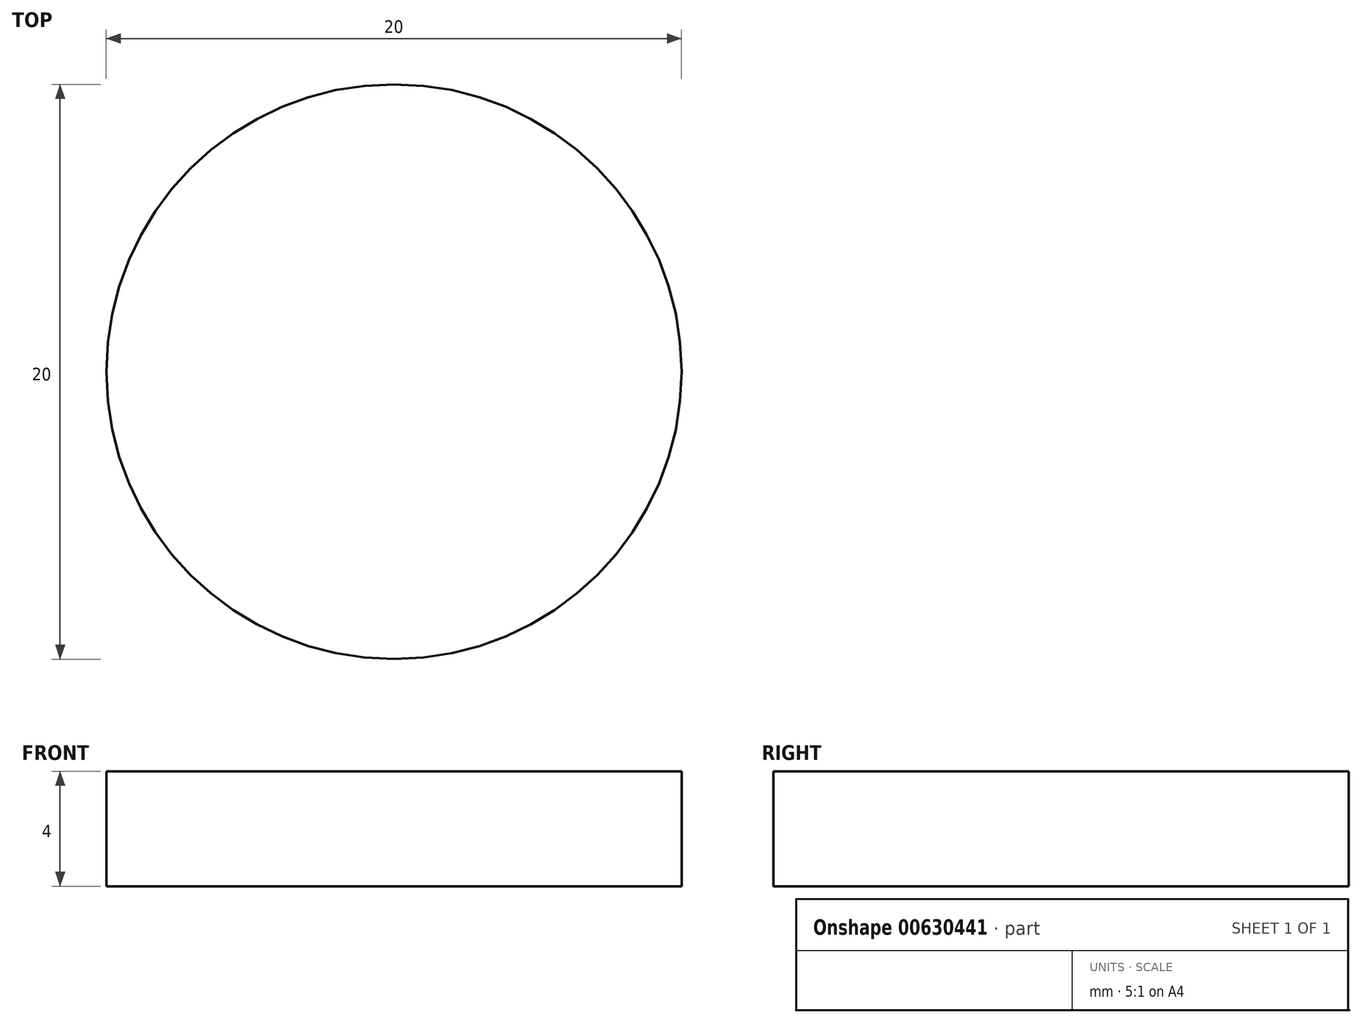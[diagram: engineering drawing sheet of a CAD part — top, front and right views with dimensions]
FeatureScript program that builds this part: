
annotation { "Feature Type Name" : "Feature", "Feature Type Description" : "" }
export const myFeature = defineFeature(function(context is Context, id is Id, definition is map)
    precondition{}
    {
        {
            var Q0;
            Q0=qCreatedBy(makeId("Top.planeOp"),FACE);
            var sketch = newSketch(context, id + "F0", { "sketchPlane" : qUnion([Q0])});
            skCircle(sketch, "E0", {"center": v(9.41, 17.38) * mm, "radius": 10 * mm});
            skSolve(sketch);
        }
        {
            var Q0;
            Q0=makeQuery(id+"F0.imprint","IMPRINT",FACE,{"disambiguationData":[TD([[makeQuery(id+"F0.imprint","IMPRINT",EDGE,{"derivedFrom":sQuery(id+"F0.wireOp",EDGE,"E0")}),1.0]])]});
            extrude(context, id + "F1", {"entities" : qUnion([Q0]), "depth" : 4 * mm, "offsetDistance" : 25 * mm});
        }
    });
